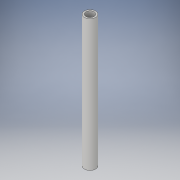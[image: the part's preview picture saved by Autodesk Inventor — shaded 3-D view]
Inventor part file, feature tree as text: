
AUTODESK INVENTOR PART (.ipt)
format: ipt  version: 2019.4 (Build 234330000, 330)  size: 93,184 bytes
history: native  units: mm
features: extrude x1, sketch x1
ambient origin geometry x8: Origin, YZ Plane, XZ Plane, XY Plane, X Axis, Y Axis, Z Axis, Center Point
bodies: Solid1 (feature_tree)
feature tree (2):
  extrude  "Extrusion1"  Depth=81.0mm
  sketch  "Sketch1"  dims[d0=5.0mm d1=7.0mm d2=81.0mm d3=0.0mm]
